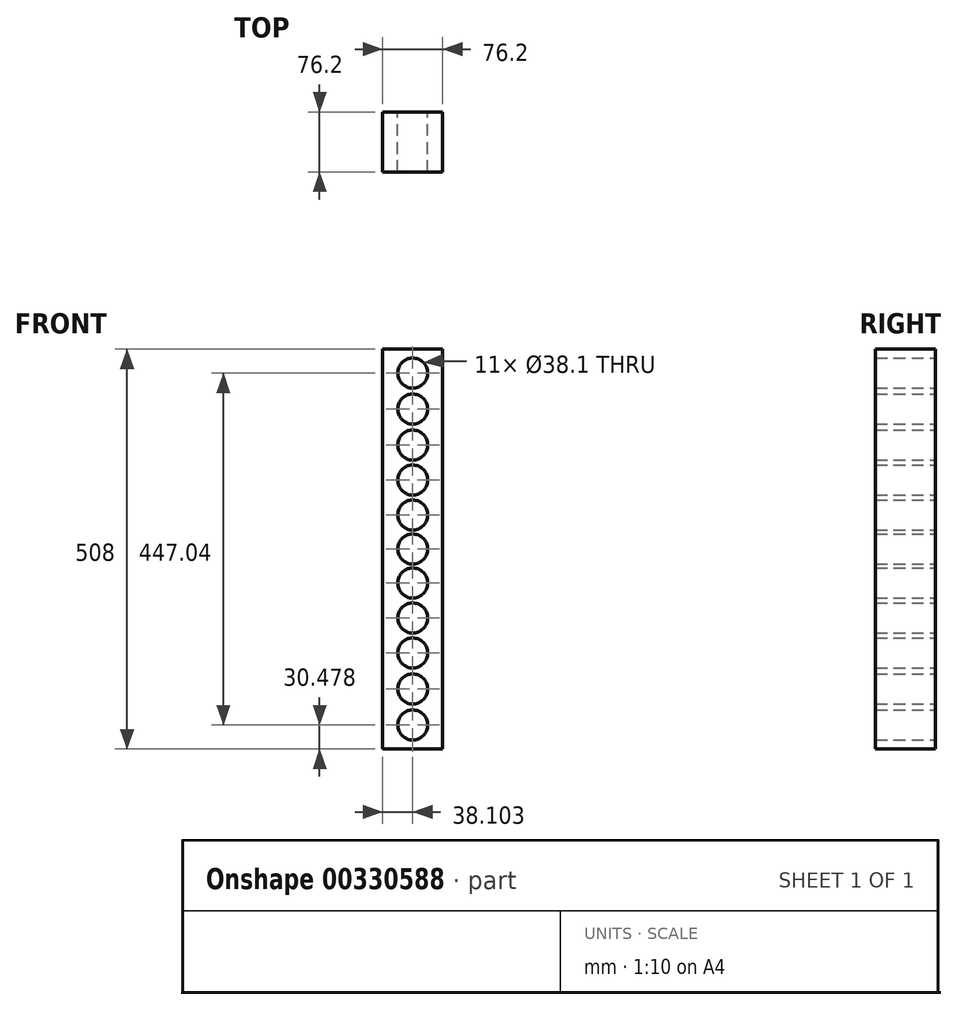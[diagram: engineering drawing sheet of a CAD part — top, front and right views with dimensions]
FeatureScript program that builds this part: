
annotation { "Feature Type Name" : "Feature", "Feature Type Description" : "" }
export const myFeature = defineFeature(function(context is Context, id is Id, definition is map)
    precondition{}
    {
        {
            var Q0;
            Q0=qCreatedBy(makeId("Front.planeOp"),FACE);
            var sketch = newSketch(context, id + "F0", { "sketchPlane" : qUnion([Q0])});
            skLineSegment(sketch, "E0.bottom", {"start": v(-149.13, 400.43) * mm, "end": v(-72.93, 400.43) * mm});
            skLineSegment(sketch, "E0.top", {"start": v(-149.13, -107.57) * mm, "end": v(-72.93, -107.57) * mm});
            skLineSegment(sketch, "E0.left", {"start": v(-149.13, 400.43) * mm, "end": v(-149.13, -107.57) * mm});
            skLineSegment(sketch, "E0.right", {"start": v(-72.93, 400.43) * mm, "end": v(-72.93, -107.57) * mm});
            skCircle(sketch, "E1", {"center": v(-111.03, 369.95) * mm, "radius": 19.05 * mm});
            skPoint(sketch, "E1.centerSnap0", {"position": v(-111.03, 400.43) * mm});
            skCircle(sketch, "E2", {"center": v(-111.03, 324.23) * mm, "radius": 19.05 * mm});
            skCircle(sketch, "E3", {"center": v(-111.03, 278.5) * mm, "radius": 19.05 * mm});
            skCircle(sketch, "E4", {"center": v(-111.03, 234.06) * mm, "radius": 19.05 * mm});
            skPoint(sketch, "E4.centerSnap0", {"position": v(-111.03, -107.57) * mm});
            skCircle(sketch, "E5", {"center": v(-111.03, 189.6) * mm, "radius": 19.05 * mm});
            skPoint(sketch, "E6.startSnap0", {"position": v(-149.13, 146.43) * mm});
            skCircle(sketch, "E7.MirrorC", {"center": v(-111.03, 103.25) * mm, "radius": 19.05 * mm});
            skCircle(sketch, "E8.MirrorC", {"center": v(-111.03, 58.8) * mm, "radius": 19.05 * mm});
            skCircle(sketch, "E9.MirrorC", {"center": v(-111.03, 14.35) * mm, "radius": 19.05 * mm});
            skCircle(sketch, "E10.MirrorC", {"center": v(-111.03, -31.37) * mm, "radius": 19.05 * mm});
            skCircle(sketch, "E11.MirrorC", {"center": v(-111.03, -77.1) * mm, "radius": 19.05 * mm});
            skCircle(sketch, "E12", {"center": v(-111.03, 146.43) * mm, "radius": 19.05 * mm});
            skPoint(sketch, "E12.centerSnap0", {"position": v(-72.93, 146.43) * mm});
            skSolve(sketch);
        }
        {
            var Q0;
            Q0 = qSketchRegion(id + "F0", true);
            extrude(context, id + "F1", {"entities" : qUnion([Q0]), "depth" : 76.2 * mm});
        }
    });
